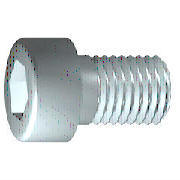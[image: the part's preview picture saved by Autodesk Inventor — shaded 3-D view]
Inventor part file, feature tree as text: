
AUTODESK INVENTOR PART (.ipt)
format: ipt  version: 2020 (Build 240168000, 168)  size: 190,464 bytes
history: native  units: mm (DEFAULTED — no unit token found)
features: sketch x2, other x1, extrude x1, plane x1, fillet x1
ambient origin geometry x7: Origin, YZ Plane, XY Plane, X Axis, Y Axis, Z Axis, Center Point
bodies: Solid1 (feature_tree)
feature tree (6):
  other  "Bryła"
  extrude  "Szczelina"  Depth=14.5mm
  plane  "Work Plane1"
  fillet  "Fillet2"  Radius=0.306825mm
  sketch  "Szkic1"
  sketch  "Szkic2"
